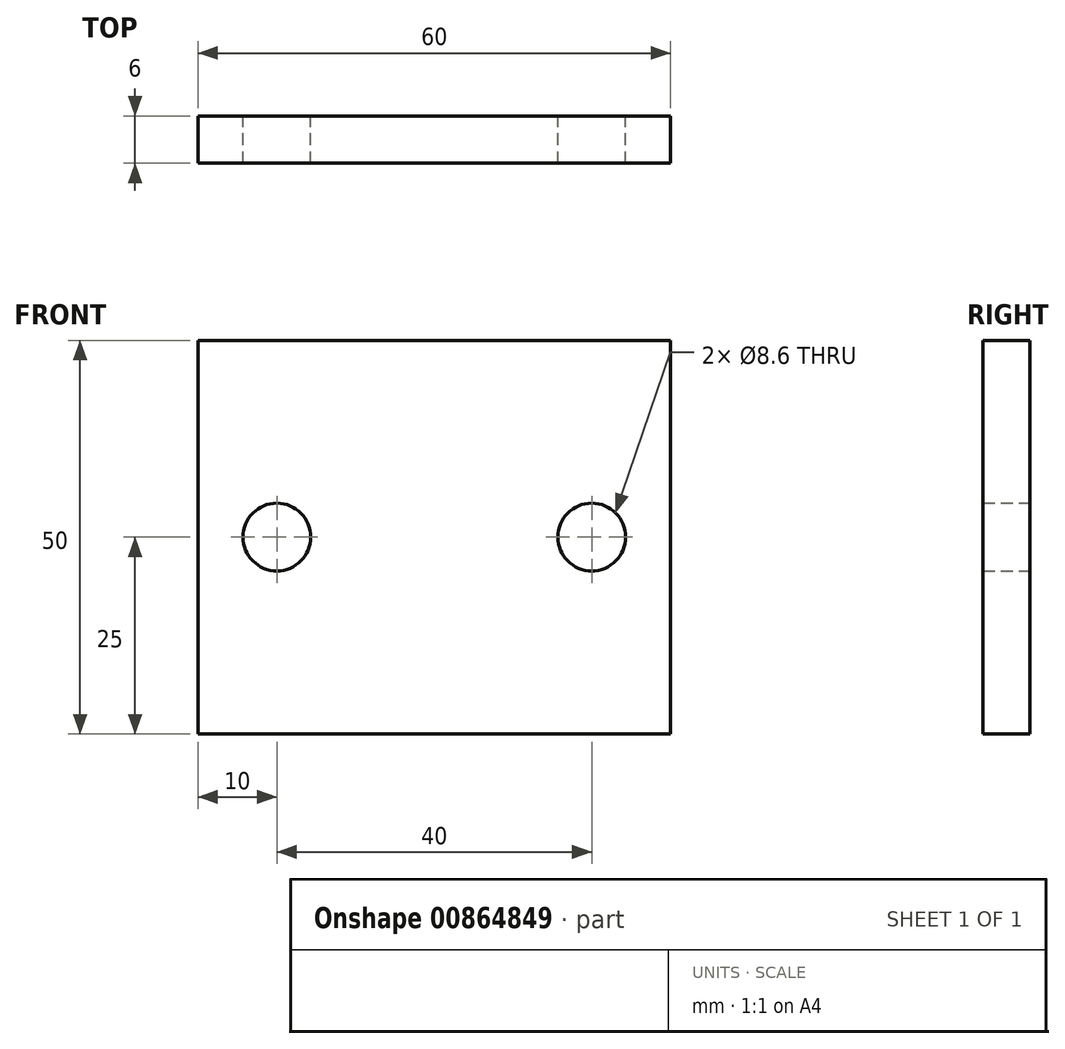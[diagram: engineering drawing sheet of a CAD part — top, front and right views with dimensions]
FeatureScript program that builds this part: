
annotation { "Feature Type Name" : "Feature", "Feature Type Description" : "" }
export const myFeature = defineFeature(function(context is Context, id is Id, definition is map)
    precondition{}
    {
        {
            var Q0;
            Q0=qCreatedBy(makeId("Front.planeOp"),FACE);
            var sketch = newSketch(context, id + "F0", { "sketchPlane" : qUnion([Q0])});
            skLineSegment(sketch, "E0.bottom", {"start": v(30, 25) * mm, "end": v(-30, 25) * mm});
            skLineSegment(sketch, "E0.top", {"start": v(30, -25) * mm, "end": v(-30, -25) * mm});
            skLineSegment(sketch, "E0.left", {"start": v(30, 25) * mm, "end": v(30, -25) * mm});
            skLineSegment(sketch, "E0.right", {"start": v(-30, 25) * mm, "end": v(-30, -25) * mm});
            skPoint(sketch, "E0.middle", {"position": v(0, 0) * mm});
            skCircle(sketch, "E1", {"center": v(-20, 0) * mm, "radius": 4.3 * mm});
            skCircle(sketch, "E2", {"center": v(20, 0) * mm, "radius": 4.3 * mm});
            skSolve(sketch);
        }
        {
            var Q0;
            Q0=makeQuery(id+"F0.imprint","IMPRINT",FACE,{"disambiguationData":[TD([[makeQuery(id+"F0.imprint","IMPRINT",EDGE,{"derivedFrom":sQuery(id+"F0.wireOp",EDGE,"E0.bottom")}),1.0]])]});
            extrude(context, id + "F1", {"entities" : qUnion([Q0]), "depth" : 6 * mm, "offsetDistance" : 25 * mm});
        }
    });
